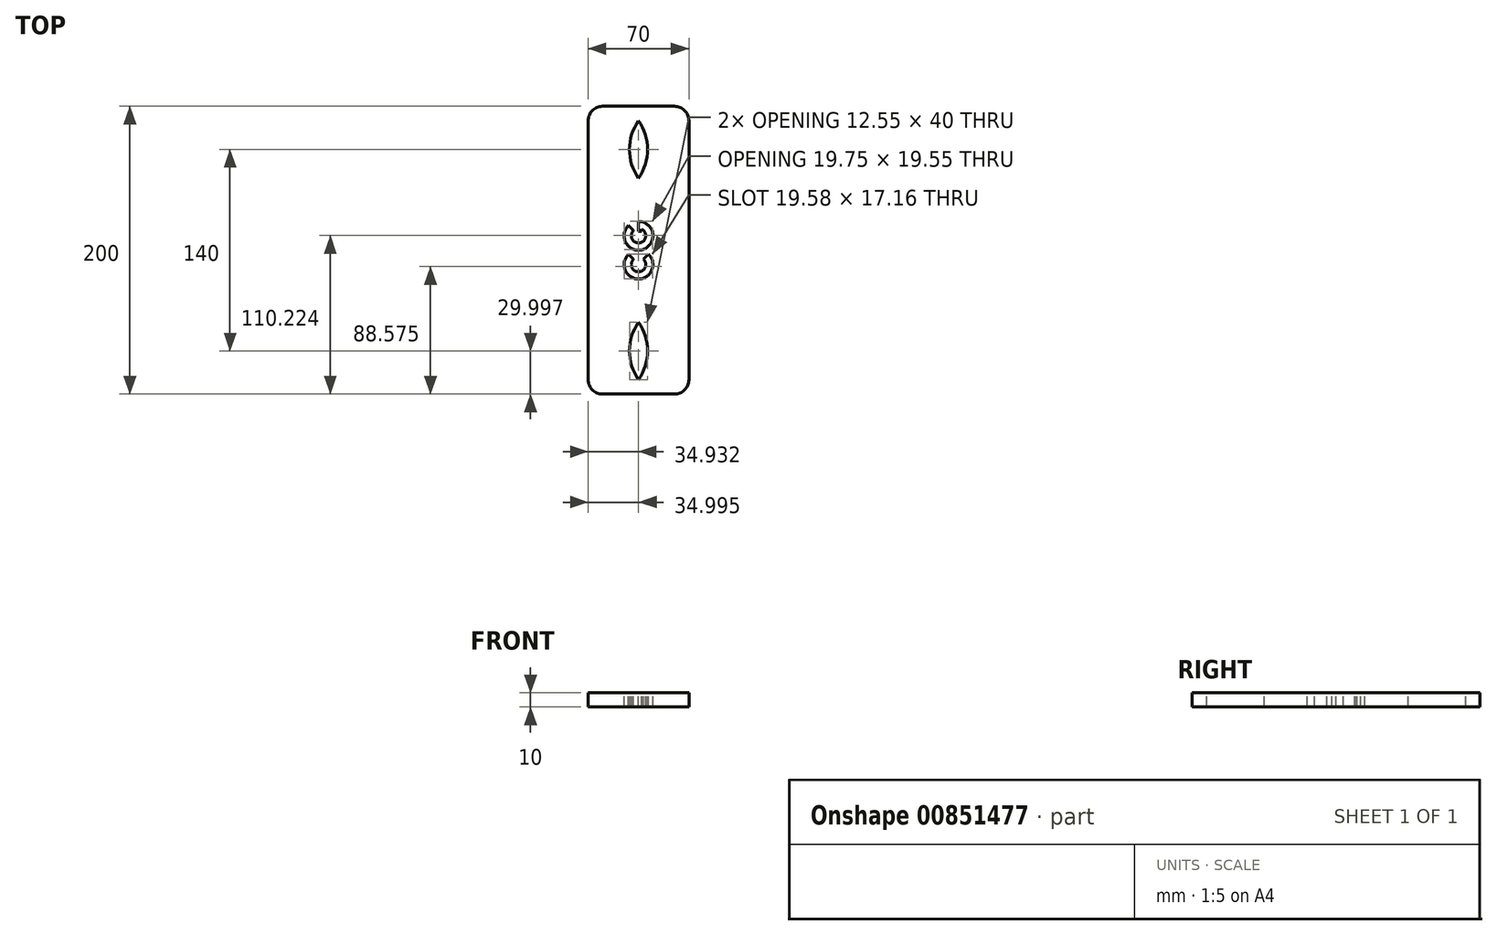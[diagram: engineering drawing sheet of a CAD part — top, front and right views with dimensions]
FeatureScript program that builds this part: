
annotation { "Feature Type Name" : "Feature", "Feature Type Description" : "" }
export const myFeature = defineFeature(function(context is Context, id is Id, definition is map)
    precondition{}
    {
        {
            var Q0;
            Q0=qCreatedBy(makeId("Top.planeOp"),FACE);
            var sketch = newSketch(context, id + "F0", { "sketchPlane" : qUnion([Q0])});
            skLineSegment(sketch, "E0", {"start": v(-21.64, 139.52) * mm, "end": v(48.36, 139.52) * mm});
            skLineSegment(sketch, "E1", {"start": v(-21.64, 139.52) * mm, "end": v(-21.64, -60.48) * mm});
            skLineSegment(sketch, "E2", {"start": v(-21.64, -60.48) * mm, "end": v(48.36, -60.48) * mm});
            skLineSegment(sketch, "E3", {"start": v(48.36, -60.48) * mm, "end": v(48.36, 139.52) * mm});
            skSolve(sketch);
        }
        {
            var Q0;
            Q0 = qSketchRegion(id + "F0", true);
            extrude(context, id + "F1", {"entities" : qUnion([Q0]), "depth" : 10 * mm, "offsetDistance" : 25 * mm});
        }
        {
            var Q0;
            Q0=makeQuery(id+"F1.opExtrude","CAP_FACE",FACE,{"disambiguationData":[OSD([sQuery(id+"F0.wireOp",EDGE,"E0"),sQuery(id+"F0.wireOp",EDGE,"E1"),sQuery(id+"F0.wireOp",EDGE,"E2"),sQuery(id+"F0.wireOp",EDGE,"E3")])],"isStart":false});
            var sketch = newSketch(context, id + "F2", { "sketchPlane" : qUnion([Q0])});
            skPoint(sketch, "E4.startSnap0", {"position": v(13.36, 139.52) * mm});
            skPoint(sketch, "E4.startSnap1", {"position": v(-21.64, 39.52) * mm});
            skPoint(sketch, "E5.end.orphan", {"position": v(48.36, 39.52) * mm});
            skPoint(sketch, "E4.end.orphan", {"position": v(-21.64, 39.52) * mm});
            skPoint(sketch, "E6.end.orphan", {"position": v(13.36, -60.48) * mm});
            skPoint(sketch, "E7.start.orphan", {"position": v(13.36, 89.52) * mm});
            skPoint(sketch, "E8.end.orphan", {"position": v(13.36, 39.52) * mm});
            skPoint(sketch, "E8.start.orphan", {"position": v(13.36, -10.48) * mm});
            skArc(sketch, "E9", {"start": v(13.36, 89.52) * mm, "mid": v(19.63, 109.52) * mm, "end": v(13.36, 129.52) * mm});
            skArc(sketch, "E10", {"start": v(13.36, 129.52) * mm, "mid": v(7.08, 109.52) * mm, "end": v(13.36, 89.52) * mm});
            skArc(sketch, "E11", {"start": v(13.36, -50.48) * mm, "mid": v(19.63, -30.48) * mm, "end": v(13.36, -10.48) * mm});
            skArc(sketch, "E12", {"start": v(13.36, -10.48) * mm, "mid": v(7.08, -30.48) * mm, "end": v(13.36, -50.48) * mm});
            skPoint(sketch, "E13.orphan", {"position": v(48.36, 129.52) * mm});
            skPoint(sketch, "E14.end.orphan", {"position": v(-21.64, 129.52) * mm});
            skPoint(sketch, "E15.orphan", {"position": v(48.36, -50.48) * mm});
            skPoint(sketch, "E16.start.orphan", {"position": v(-21.64, -50.48) * mm});
            skLineSegment(sketch, "E17", {"start": v(48.36, 39.52) * mm, "end": v(-21.64, 39.52) * mm});
            skArc(sketch, "E18", {"start": v(6.37, 36.67) * mm, "mid": v(13.36, 19.52) * mm, "end": v(20.34, 36.67) * mm});
            skArc(sketch, "E19", {"start": v(6.37, 56.67) * mm, "mid": v(17.13, 40.26) * mm, "end": v(13.36, 59.52) * mm});
            skArc(sketch, "E20", {"start": v(9.91, 33.14) * mm, "mid": v(13.36, 24.52) * mm, "end": v(16.8, 33.14) * mm});
            skArc(sketch, "E21", {"start": v(9.91, 53.14) * mm, "mid": v(14.22, 44.6) * mm, "end": v(15.36, 54.1) * mm});
            skLineSegment(sketch, "E22", {"start": v(9.91, 33.14) * mm, "end": v(6.37, 36.67) * mm});
            skLineSegment(sketch, "E23", {"start": v(16.8, 33.14) * mm, "end": v(20.34, 36.67) * mm});
            skLineSegment(sketch, "E24", {"start": v(9.91, 53.14) * mm, "end": v(6.37, 56.67) * mm});
            skLineSegment(sketch, "E25", {"start": v(13.36, 54.52) * mm, "end": v(13.36, 59.52) * mm});
            skLineSegment(sketch, "E26", {"start": v(13.36, 54.52) * mm, "end": v(13.36, 52.52) * mm});
            skLineSegment(sketch, "E27", {"start": v(13.36, 52.52) * mm, "end": v(15.36, 52.52) * mm});
            skLineSegment(sketch, "E28", {"start": v(15.36, 52.52) * mm, "end": v(15.36, 54.1) * mm});
            skSolve(sketch);
        }
        {
            var Q0;
            Q0 = qSketchRegion(id + "F2", true);
            extrude(context, id + "F3", {"entities" : qUnion([Q0]), "operationType" : NewBodyOperationType.REMOVE, "oppositeDirection" : true, "depth" : 25 * mm, "offsetDistance" : 25 * mm});
        }
        {
            var Q0;
            Q0 = qSketchRegion(id + "F2", true);
            extrude(context, id + "F4", {"entities" : qUnion([Q0]), "operationType" : NewBodyOperationType.REMOVE, "oppositeDirection" : true, "depth" : 25 * mm, "offsetDistance" : 25 * mm});
        }
        {
            var Q0;
            Q0=makeQuery(id+"F1.opExtrude","SWEPT_EDGE",EDGE,{"disambiguationData":[OSD([sQuery(id+"F0.wireOp",EDGE,"E2"),sQuery(id+"F0.wireOp",EDGE,"E3")])]});
            fillet(context, id + "F5", {"entities" : qUnion([Q0]), "radius" : 10 * mm, "tangentPropagation" : true, "allowEdgeOverflow" : false});
        }
        {
            var Q0;
            Q0=makeQuery(id+"F1.opExtrude","SWEPT_EDGE",EDGE,{"disambiguationData":[OSD([sQuery(id+"F0.wireOp",EDGE,"E1"),sQuery(id+"F0.wireOp",EDGE,"E2")])]});
            var Q1;
            Q1=makeQuery(id+"F1.opExtrude","SWEPT_EDGE",EDGE,{"disambiguationData":[OSD([sQuery(id+"F0.wireOp",EDGE,"E0"),sQuery(id+"F0.wireOp",EDGE,"E1")])]});
            var Q2;
            Q2=makeQuery(id+"F1.opExtrude","SWEPT_EDGE",EDGE,{"disambiguationData":[OSD([sQuery(id+"F0.wireOp",EDGE,"E0"),sQuery(id+"F0.wireOp",EDGE,"E3")])]});
            fillet(context, id + "F6", {"entities" : qUnion([Q0, Q1, Q2]), "radius" : 10 * mm, "tangentPropagation" : true, "allowEdgeOverflow" : false});
        }
    });
